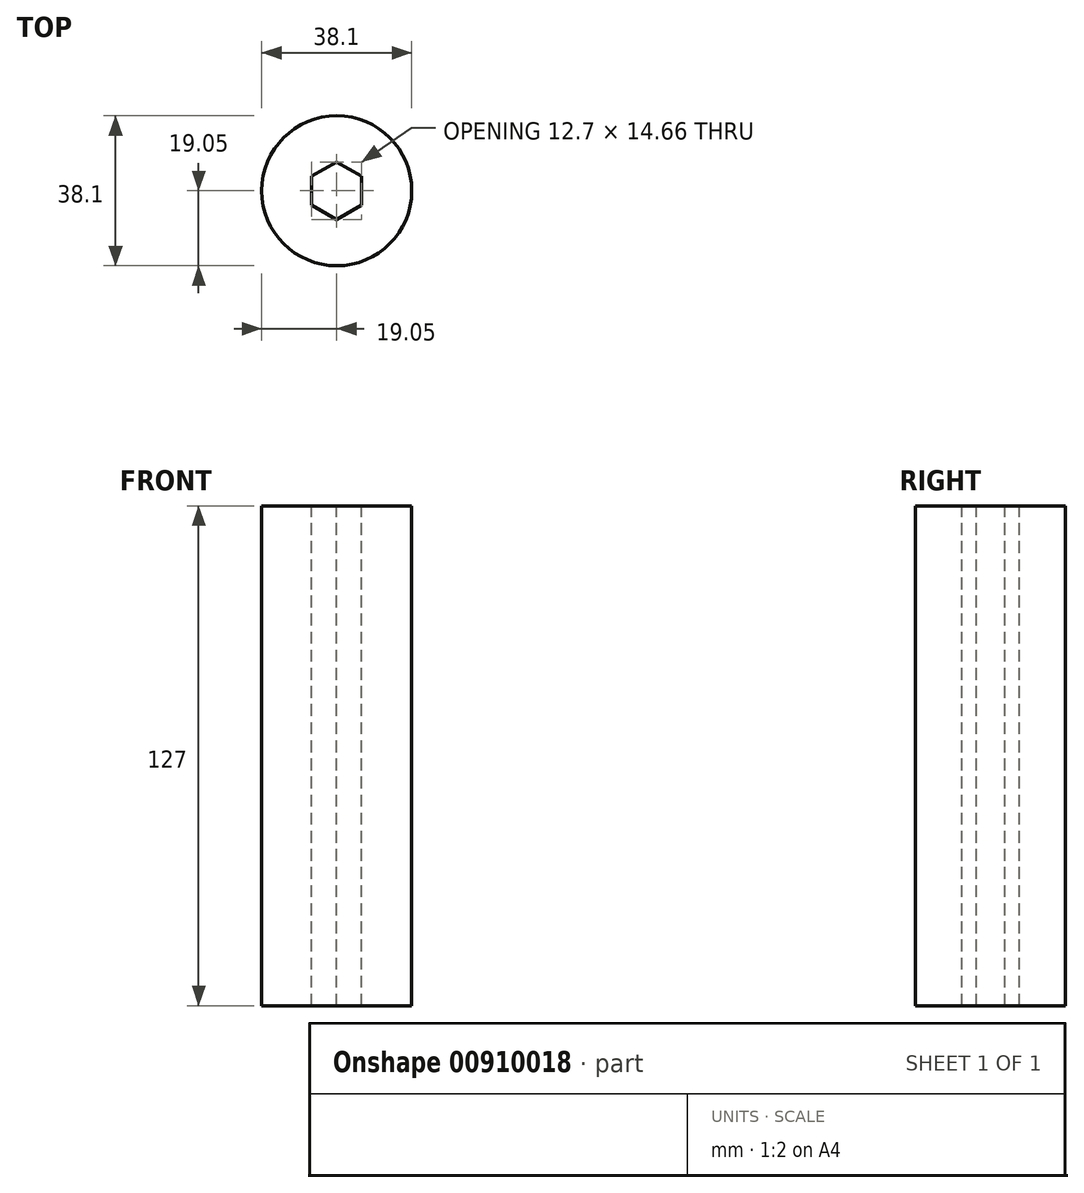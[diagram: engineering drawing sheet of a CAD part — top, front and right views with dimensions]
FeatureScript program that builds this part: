
annotation { "Feature Type Name" : "Feature", "Feature Type Description" : "" }
export const myFeature = defineFeature(function(context is Context, id is Id, definition is map)
    precondition{}
    {
        {
            var Q0;
            Q0=qCreatedBy(makeId("Top.planeOp"),FACE);
            var sketch = newSketch(context, id + "F0", { "sketchPlane" : qUnion([Q0])});
            skCircle(sketch, "E0", {"center": v(0, 0) * mm, "radius": 19.05 * mm});
            skSolve(sketch);
        }
        {
            var Q0;
            Q0=qSketchRegion(id+"F0",true);
            extrude(context, id + "F1", {"entities" : qUnion([Q0]), "depth" : 127 * mm, "offsetDistance" : 25.4 * mm});
        }
        {
            var Q0;
            Q0=makeQuery(id+"F1.opExtrude","CAP_FACE",FACE,{"disambiguationData":[OSD([sQuery(id+"F0.wireOp",EDGE,"E0")])],"isStart":false});
            var sketch = newSketch(context, id + "F2", { "sketchPlane" : qUnion([Q0])});
            skCircle(sketch, "E1.cCircle", {"center": v(0, 0) * mm, "radius": 6.35 * mm, "construction": true});
            skLineSegment(sketch, "E1.0", {"start": v(6.35, 3.67) * mm, "end": v(6.35, -3.67) * mm});
            skLineSegment(sketch, "E1.1", {"start": v(6.35, -3.67) * mm, "end": v(0, -7.33) * mm});
            skLineSegment(sketch, "E1.2", {"start": v(0, -7.33) * mm, "end": v(-6.35, -3.67) * mm});
            skLineSegment(sketch, "E1.3", {"start": v(-6.35, -3.67) * mm, "end": v(-6.35, 3.67) * mm});
            skLineSegment(sketch, "E1.4", {"start": v(-6.35, 3.67) * mm, "end": v(0, 7.33) * mm});
            skLineSegment(sketch, "E1.5", {"start": v(0, 7.33) * mm, "end": v(6.35, 3.67) * mm});
            skPoint(sketch, "E1.0.midPoint", {"position": v(6.35, 0) * mm});
            skSolve(sketch);
        }
        {
            var Q0;
            Q0=qSketchRegion(id+"F2",true);
            extrude(context, id + "F3", {"entities" : qUnion([Q0]), "operationType" : NewBodyOperationType.REMOVE, "oppositeDirection" : true, "depth" : 152.4 * mm, "offsetDistance" : 25.4 * mm});
        }
    });
